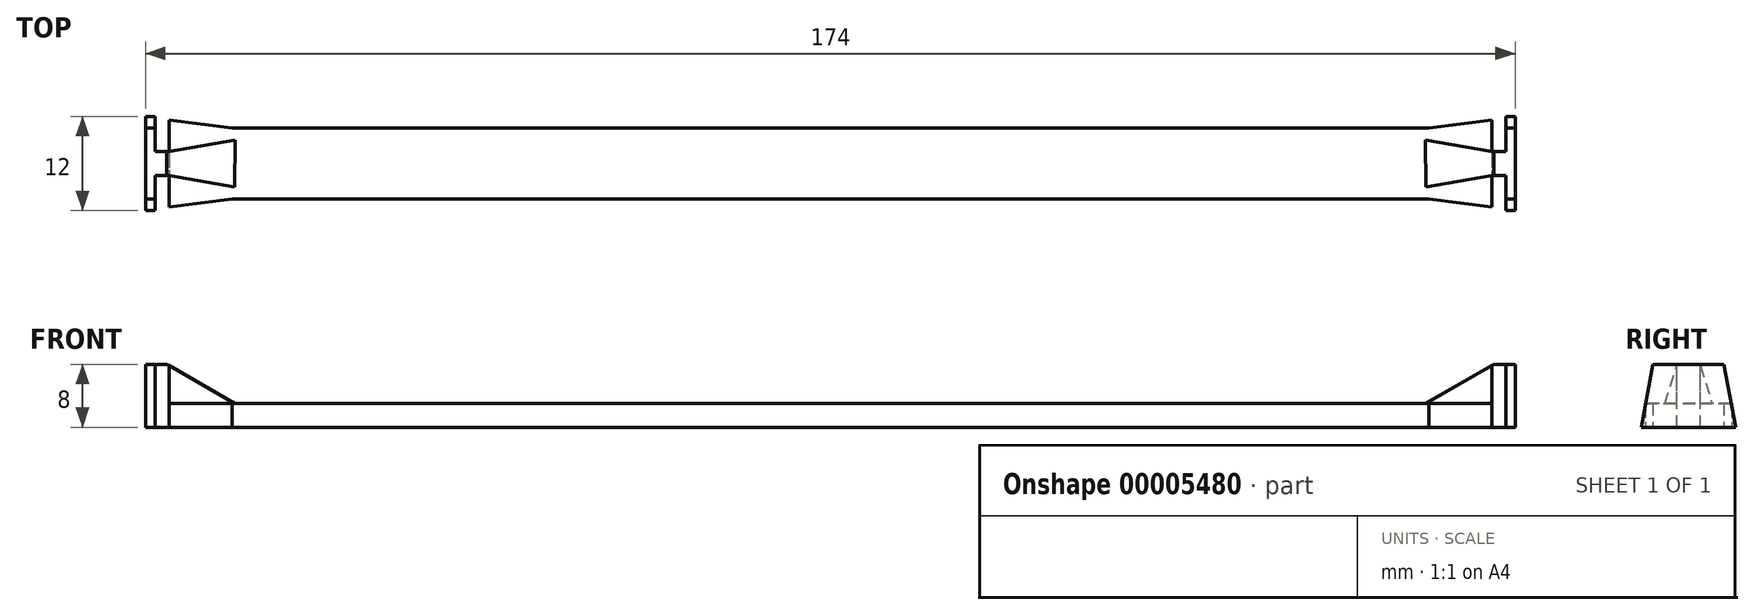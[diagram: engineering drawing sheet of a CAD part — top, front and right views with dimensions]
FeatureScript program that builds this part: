
annotation { "Feature Type Name" : "Feature", "Feature Type Description" : "" }
export const myFeature = defineFeature(function(context is Context, id is Id, definition is map)
    precondition{}
    {
        {
            var Q0;
            Q0=qCreatedBy(makeId("Top.planeOp"),FACE);
            var sketch = newSketch(context, id + "F0", { "sketchPlane" : qUnion([Q0])});
            skLineSegment(sketch, "E0.rect.bottom", {"start": v(76, -4.5) * mm, "end": v(-76, -4.5) * mm});
            skLineSegment(sketch, "E0.rect.top", {"start": v(76, 4.5) * mm, "end": v(-76, 4.5) * mm});
            skLineSegment(sketch, "E0.rect.left", {"start": v(76, -4.5) * mm, "end": v(76, 4.5) * mm});
            skLineSegment(sketch, "E0.rect.right", {"start": v(-76, -4.5) * mm, "end": v(-76, 4.5) * mm});
            skPoint(sketch, "E0.rect.middle", {"position": v(0, 0) * mm});
            skLineSegment(sketch, "E1", {"start": v(-76, 4.5) * mm, "end": v(-84, 5.5) * mm});
            skLineSegment(sketch, "E2", {"start": v(-84, 5.5) * mm, "end": v(-84, -5.5) * mm});
            skLineSegment(sketch, "E3", {"start": v(-84, -5.5) * mm, "end": v(-76, -4.5) * mm});
            skLineSegment(sketch, "E4", {"start": v(76, -4.5) * mm, "end": v(84, -5.5) * mm});
            skLineSegment(sketch, "E5", {"start": v(84, -5.5) * mm, "end": v(84, 5.5) * mm});
            skLineSegment(sketch, "E6", {"start": v(84, 5.5) * mm, "end": v(76, 4.5) * mm});
            skLineSegment(sketch, "E7", {"start": v(0, 0) * mm, "end": v(106.48, 0) * mm, "construction": true});
            skSolve(sketch);
        }
        {
            var Q0;
            Q0=makeQuery(id+"F0.imprint","IMPRINT",FACE,{"disambiguationData":[TD([[makeQuery(id+"F0.imprint","IMPRINT",EDGE,{"derivedFrom":sQuery(id+"F0.wireOp",EDGE,"E0.rect.left")}),-1.0]])]});
            var Q1;
            Q1=makeQuery(id+"F0.imprint","IMPRINT",FACE,{"disambiguationData":[TD([[makeQuery(id+"F0.imprint","IMPRINT",EDGE,{"derivedFrom":sQuery(id+"F0.wireOp",EDGE,"E0.rect.right")}),1.0]])]});
            var Q2;
            Q2=makeQuery(id+"F0.imprint","IMPRINT",FACE,{"disambiguationData":[TD([[makeQuery(id+"F0.imprint","IMPRINT",EDGE,{"derivedFrom":sQuery(id+"F0.wireOp",EDGE,"E0.rect.bottom")}),-1.0]])]});
            extrude(context, id + "F1", {"entities" : qUnion([Q0, Q1, Q2]), "depth" : 3 * mm});
        }
        {
            var Q0;
            Q0=makeQuery(id+"F1.opExtrude","SWEPT_FACE",FACE,{"disambiguationData":[OSD([sQuery(id+"F0.wireOp",EDGE,"E5")])]});
            var sketch = newSketch(context, id + "F2", { "sketchPlane" : qUnion([Q0])});
            skLineSegment(sketch, "E8.bottom", {"start": v(-1.5, 0) * mm, "end": v(1.5, 0) * mm});
            skLineSegment(sketch, "E8.top", {"start": v(-1.5, 8) * mm, "end": v(1.5, 8) * mm});
            skLineSegment(sketch, "E8.left", {"start": v(-1.5, 0) * mm, "end": v(-1.5, 8) * mm});
            skLineSegment(sketch, "E8.right", {"start": v(1.5, 0) * mm, "end": v(1.5, 8) * mm});
            skLineSegment(sketch, "E9", {"start": v(0, 0) * mm, "end": v(0, 9.7) * mm, "construction": true});
            skSolve(sketch);
        }
        {
            var Q0;
            Q0 = qSketchRegion(id + "F2", true);
            extrude(context, id + "F3", {"entities" : qUnion([Q0]), "operationType" : NewBodyOperationType.ADD, "depth" : 1.8 * mm});
        }
        {
            var Q0;
            Q0=makeQuery(id+"F3.opExtrude","CAP_FACE",FACE,{"disambiguationData":[OSD([sQuery(id+"F2.wireOp",EDGE,"E8.bottom"),sQuery(id+"F2.wireOp",EDGE,"E8.top"),sQuery(id+"F2.wireOp",EDGE,"E8.left"),sQuery(id+"F2.wireOp",EDGE,"E8.right")])],"isStart":false});
            var sketch = newSketch(context, id + "F4", { "sketchPlane" : qUnion([Q0])});
            skLineSegment(sketch, "E10.bottom", {"start": v(-6, 0) * mm, "end": v(6, 0) * mm});
            skLineSegment(sketch, "E10.top", {"start": v(-4.5, 8) * mm, "end": v(4.5, 8) * mm});
            skLineSegment(sketch, "E10.left", {"start": v(-6, 0) * mm, "end": v(-4.5, 8) * mm});
            skLineSegment(sketch, "E10.right", {"start": v(6, 0) * mm, "end": v(4.5, 8) * mm});
            skLineSegment(sketch, "E11", {"start": v(0, 8) * mm, "end": v(0, -8.1) * mm, "construction": true});
            skSolve(sketch);
        }
        {
            var Q0;
            Q0 = qSketchRegion(id + "F4", true);
            extrude(context, id + "F5", {"entities" : qUnion([Q0]), "operationType" : NewBodyOperationType.ADD, "depth" : 1.2 * mm});
        }
        {
            var Q0;
            Q0=makeQuery(id+"F1.opExtrude","CAP_FACE",FACE,{"disambiguationData":[OSD([sQuery(id+"F0.wireOp",EDGE,"E0.rect.bottom"),sQuery(id+"F0.wireOp",EDGE,"E0.rect.top"),sQuery(id+"F0.wireOp",EDGE,"E1"),sQuery(id+"F0.wireOp",EDGE,"E2"),sQuery(id+"F0.wireOp",EDGE,"E3"),sQuery(id+"F0.wireOp",EDGE,"E4"),sQuery(id+"F0.wireOp",EDGE,"E5"),sQuery(id+"F0.wireOp",EDGE,"E6")])],"isStart":false});
            var sketch = newSketch(context, id + "F6", { "sketchPlane" : qUnion([Q0])});
            skLineSegment(sketch, "E12", {"start": v(84, -1.5) * mm, "end": v(75.66, -3) * mm});
            skLineSegment(sketch, "E13", {"start": v(75.61, 3) * mm, "end": v(84, 1.5) * mm});
            skLineSegment(sketch, "E14", {"start": v(71.62, 0) * mm, "end": v(89.63, 0) * mm, "construction": true});
            skLineSegment(sketch, "E15", {"start": v(75.66, -3) * mm, "end": v(75.61, 3) * mm});
            skSolve(sketch);
        }
        {
            var Q0;
            Q0 = qSketchRegion(id + "F6", true);
            var Q1;
            Q1=makeQuery(id+"F6.imprint","IMPRINT",FACE,{"disambiguationData":[TD([[makeQuery(id+"F6.imprint","IMPRINT",EDGE,{"derivedFrom":sQuery(id+"F6.wireOp",EDGE,"E12")}),-1.0]])]});
            var Q2;
            Q2=makeQuery(id+"F5.boolean.opBoolean","MERGE",FACE,{"derivedFrom":[makeQuery(id+"F3.opExtrude","SWEPT_FACE",FACE,{"disambiguationData":[OSD([sQuery(id+"F2.wireOp",EDGE,"E8.top")])]}),makeQuery(id+"F5.opExtrude","SWEPT_FACE",FACE,{"disambiguationData":[OSD([sQuery(id+"F4.wireOp",EDGE,"E10.top")])]})]});
            extrude(context, id + "F7", {"entities" : qUnion([Q0, Q1]), "operationType" : NewBodyOperationType.ADD, "endBound" : BoundingType.UP_TO_SURFACE, "endBoundEntityFace" : qUnion([Q2]), "depth" : 3.06 * mm});
        }
        {
            var Q0;
            Q0=makeQuery(id+"F7.opExtrude","CAP_EDGE",EDGE,{"disambiguationData":[OSD([sQuery(id+"F6.wireOp",EDGE,"E15")])],"isStart":false});
            chamfer(context, id + "F8", {"entities" : qUnion([Q0]), "chamferType" : ChamferType.OFFSET_ANGLE, "width" : 5 * mm, "oppositeDirection" : false, "angle" : 60 * degree, "tangentPropagation" : true});
        }
        {
            var Q0;
            Q0=makeQuery(id+"F1.opExtrude","SWEPT_BODY",BODY,{"disambiguationData":[OSD([sQuery(id+"F0.wireOp",EDGE,"E0.rect.bottom"),sQuery(id+"F0.wireOp",EDGE,"E0.rect.top"),sQuery(id+"F0.wireOp",EDGE,"E1"),sQuery(id+"F0.wireOp",EDGE,"E2"),sQuery(id+"F0.wireOp",EDGE,"E3"),sQuery(id+"F0.wireOp",EDGE,"E4"),sQuery(id+"F0.wireOp",EDGE,"E5"),sQuery(id+"F0.wireOp",EDGE,"E6")])]});
            var Q1;
            Q1=qCreatedBy(makeId("Right.planeOp"),FACE);
            mirror(context, id + "F9", {"entities" : qUnion([Q0]), "mirrorPlane" : qUnion([Q1])});
        }
    });
